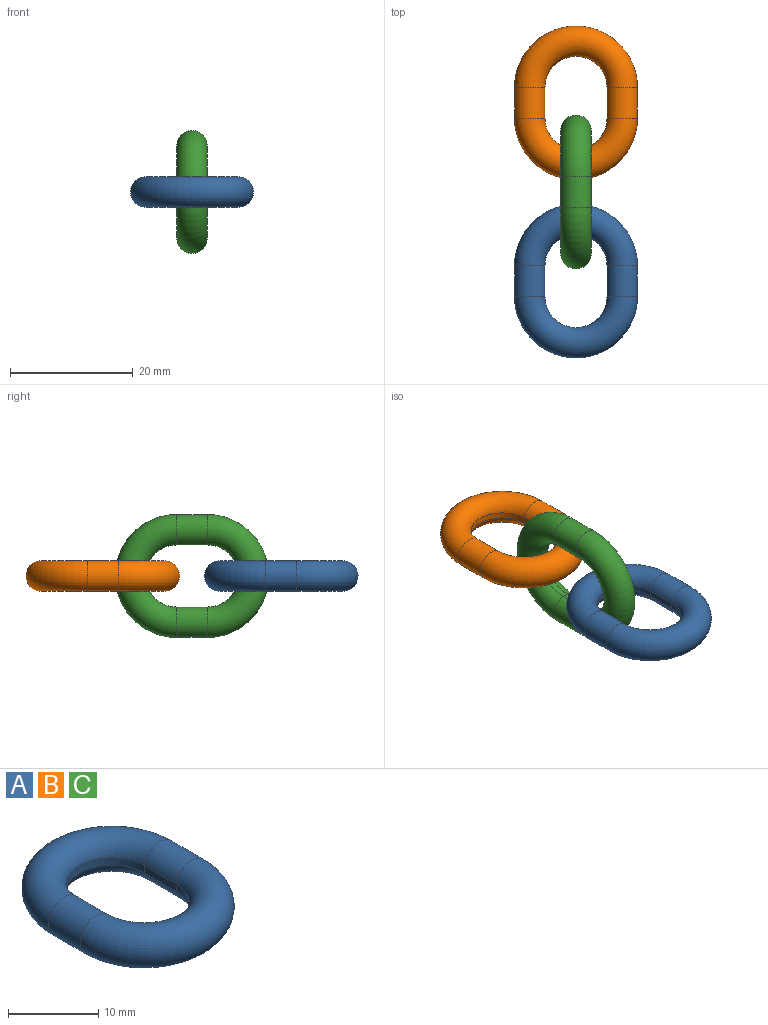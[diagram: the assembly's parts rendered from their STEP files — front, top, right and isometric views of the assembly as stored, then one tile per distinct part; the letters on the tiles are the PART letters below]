
ASSEMBLY  parts=3 mates=2
PART A: 8 faces, bbox 21.6x26.6x5 mm
  f0: plane 5x1mm, normal (1,0,0), area 5mm2, adj f1,f2,f6
  f1: cylinder r=2.5mm len=5mm, axis (0,1,0), area 73.5mm2, adj f0,f3,f7
  f2: cylinder r=5.05mm len=10.1mm, axis (0,0,-1), area 15.9mm2, adj f0,f3,f4
  f3: torus R=7.5mm, axis (0,0,-1), area 354.2mm2, adj f1,f2,f5
  f4: plane 5x1mm, normal (-1,0,0), area 5mm2, adj f2,f5,f6
  f5: cylinder r=2.5mm len=5mm, axis (0,-1,0), area 73.5mm2, adj f3,f4,f7
  f6: cylinder r=5.05mm len=10.1mm, axis (0,0,-1), area 15.9mm2, adj f0,f4,f7
  f7: torus R=7.5mm, axis (0,0,-1), area 354.2mm2, adj f1,f5,f6
PART B: same geometry as A
PART C: same geometry as A
PLACE A rot(axis=(0,0,1),180deg) t=(-33.78,13.65,6.49)mm
PLACE B rot(axis=(0,0,1),180deg) t=(-33.78,42.65,6.49)mm
PLACE C rot(axis=(0,1,0),90deg) t=(-33.78,33.15,6.49)mm
MATE planar A.f4 <-> C.f2  axis (1,0,0) through (-38.83,16.15,6.49)mm
MATE parallel B.f0 <-> A.f0  axis (-1,0,0) through (-28.73,45.15,6.49)mm
